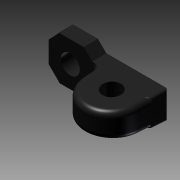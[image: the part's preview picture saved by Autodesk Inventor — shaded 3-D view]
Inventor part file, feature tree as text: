
AUTODESK INVENTOR PART (.ipt)
format: ipt  version: 2012 (Build 160160000, 160)  size: 438,784 bytes
history: native  units: in
note: dims shown in document units (in); Inventor stores cm internally (conversion verified against a paired STEP export)
features: other x1, imported_body x1, plane x1, split x1, fillet x1
ambient origin geometry x8: Origin, YZ Plane, XZ Plane, XY Plane, X Axis, Y Axis, Z Axis, Center Point
feature tree (5):
  parser-record x1  (decoder bookkeeping rows leaked as tree rows — omitted from the tree; the rows remain in map.json)
  imported_body  "Base1"
  plane  "Work Plane1"
  split  "Split1"
  fillet  "Fillet1"  [1 undecoded]
note: 1 required parameter value undecoded (feature->parameter linkage not recoverable at this tier; creation-order binding heuristic only, values carry confidence <= 0.55)
